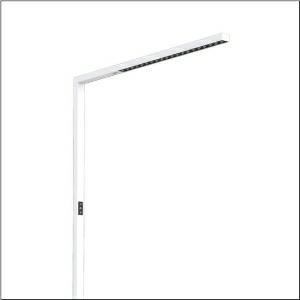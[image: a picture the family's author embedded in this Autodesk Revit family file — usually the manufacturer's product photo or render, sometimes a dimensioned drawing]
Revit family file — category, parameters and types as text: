
# Revit family: silica_31_floor_51my52fa4cw
name_source: partatom
category: Lighting Fixtures
units: mm (PartAtom-declared; Revit-internal decimal feet)

## family parameters
Cut with Voids When Loaded = No
Host = Face
Light Source = No
Part Type = Normal
Room Calculation Point = No
Round Connector Dimension = Use Diameter
Shared = No

## types (1)
- Silica 31 Floor (1 x LED, 10600 lm, 75 W, 4000K)
    Apparent Load = 75 VA
    CIE Flux Codes = 86 100 100 24 100
    Color Rendering = 80
    Color Temperature = 4000K
    Default Elevation = 1800 mm
    Description = Silica® 31 Floor, floorstanding luminaire, secondary optical cover: cover panel, of PMMA, light emission: direct/indirect distribution, primary light characteristic: symmetric, installation type: not mounted, LED, rated luminous flux: 10.600lm, luminous efficacy: 141lm/W, light colour: 840, colour temperature: 4000K, control gear: Touchdim, daylight-dependent control, with cable with plug, mains connection: 230V, AC, 50Hz, connection cable included, cable length: 2,5m, rated input power: 75W, luminaire head, of aluminium, traffic white (RAL 9016), length: 1.203mm, width: 52mm, supporting column, angular, of aluminium, traffic white (RAL 9016), baseplate, of steel, traffic white (RAL 9016), local control - self-sufficient standalone sensors, direct and indirect component separately switchable, protection rating (complete): IP20, insulation class (complete): insulation class I (protective earthing), certification: CE, ENEC, permissible operating ambient temperature: -20..+40°C, standard: EN 50419, packaging unit: 1 piece
    Height = 36 mm
    Lamp = 1 x LED
    Lamp Light Flux = 10600 lm
    Lamp Power = 75 W
    Lamp count = 1
    Length = 1203 mm
    Luminous efficacy = 141 lm/W
    Manufacturer = Siteco
    ModVariant = No
    Model = 51MY52FA4CW
    Mounting Place = Floor
    Mounting Type = Freestanding
    Number of Poles = 1
    OnlyDefault = Yes
    Power Factor = 1
    Product Name = Silica 31 Floor
    Product group = floorstanding luminaire
    ProductGroupID = 1302
    Protection Class = Protection class I
    Protection Degree = IP 20
    RLX_Detail_Level = 1
    RLX_Emergency_Light_Flux = 0 lm
    RLX_Emergency_Type = 0
    RLX_Emergency_Type_DB = No
    RlxData = <blob elided: 17313 chars, md5=388f46d4>
    Socket = socket
    Standby Power = 0 W
    System Light Flux = 10600 lm
    System Power = 75 W
    Type Comments = Product without accessories
    Type Image = l_1275309.jpg
    URL = http://relux.com
    VarID = ---
    Voltage = 0 V
    Weight = 0.00 kg
    Width = 52 mm  [stored 0.170604 ft]

note: [stored X ft] marks values corroborated as IEEE doubles in the binary element streams (Revit-internal decimal feet)

## geometry (parser evidence)
native form markers: Blend x4, Sweep x17
no freeform markers — native parametric forms only
